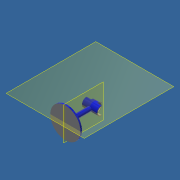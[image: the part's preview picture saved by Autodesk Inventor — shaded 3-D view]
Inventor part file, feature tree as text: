
AUTODESK INVENTOR PART (.ipt)
format: ipt  version: 2018 (Build 220112000, 112)  size: 217,088 bytes
history: native  units: mm
features: extrude x7, sketch x7, plane x2, fillet x1, mirror x1, projected_geometry x1
ambient origin geometry x8: Origin, YZ Plane, XZ Plane, XY Plane, X Axis, Y Axis, Z Axis, Center Point
bodies: Solid1 (feature_tree)
feature tree (19):
  extrude  "Extrusion1"  Depth=10.0mm TaperAngle=0.0deg
  extrude  "Extrusion2"  Depth=30.0mm
  fillet  "Fillet1"  Radius=20.0mm
  extrude  "Extrusion3"  Depth=60.0mm
  extrude  "Extrusion5"  Depth=30.0mm TaperAngle=0.0deg
  plane  "Work Plane1"
  extrude  "Extrusion6"  Depth=2.0mm
  plane  "Work Plane2"
  mirror  "Mirror1"
  extrude  "Extrusion7"  Depth=5.0mm
  extrude  "Extrusion8"  Depth=3.0mm
  sketch  "Sketch1"  dims[d0=200.0mm d1=10.0mm d2=0.0mm]
  sketch  "Sketch2"  dims[d3=150.0mm d4=0.0mm d5=30.0mm d6=20.0mm]
  sketch  "Sketch3"  dims[d7=50.0mm d8=60.0mm]
  sketch  "Sketch5"  dims[d9=40.0mm d10=0.0mm d14=30.0mm d15=0.0mm]
  projected_geometry  "Projected Loop1"
  sketch  "Sketch7"  dims[d16=2.0mm d17=2.0mm]
  sketch  "Sketch8"  dims[d18=5.0mm d19=5.0mm]
  sketch  "Sketch9"  dims[d20=3.0mm d21=3.0mm d22=30.0mm d23=0.0mm d24=5.0mm d25=0.0mm d26=2.0mm d27=2.0mm d28=2.0mm d29=5.0mm d30=0.0mm]
